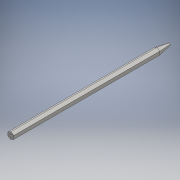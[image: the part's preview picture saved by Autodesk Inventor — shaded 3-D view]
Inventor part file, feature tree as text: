
AUTODESK INVENTOR PART (.ipt)
format: ipt  version: 2016 (Build 200138000, 138)  size: 121,344 bytes
history: native  units: mm
features: sketch x3, extrude x1, plane x1, loft x1, hole x1, other x1
ambient origin geometry x8: Origin, YZ Plane, XZ Plane, XY Plane, X Axis, Y Axis, Z Axis, Center Point
bodies: Solid1 (feature_tree)
feature tree (8):
  extrude  "Extrusion1"  Depth=120.0mm TaperAngle=0.0deg
  plane  "Work Plane1"
  sketch  "Sketch2"  dims[d3=10.0mm d4=4.9mm]
  loft  "Loft1"
  hole  "Hole1"  [1 undecoded]
  sketch  "Sketch1"  dims[d0=4.9mm d1=120.0mm d2=0.0mm]
  sketch  "Sketch3"  dims[d5=2.0mm d6=0.0mm d7=90.0deg d8=0.0mm d9=90.0deg d10=10.0mm d11=10.0mm d12=1.5mm d13=6.0mm d14=4.0mm d15=2.0mm d16=90.0deg d17=8.0mm d18=20.594885mm]
  other  "Edges1"
note: 1 required parameter value undecoded (feature->parameter linkage not recoverable at this tier; creation-order binding heuristic only, values carry confidence <= 0.55)
